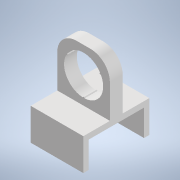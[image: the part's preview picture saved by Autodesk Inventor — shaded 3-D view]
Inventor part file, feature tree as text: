
AUTODESK INVENTOR PART (.ipt)
format: ipt  version: 2022 (Build 260153000, 153)  size: 176,128 bytes
history: native  units: mm
features: other x5, reference x4, extrude x3, sketch x3, fillet x1
ambient origin geometry x8: Origin, YZ Plane, XZ Plane, XY Plane, X Axis, Y Axis, Z Axis, Center Point
bodies: Solid1 (feature_tree)
feature tree (16):
  extrude  "Extrusion1"  Depth=0.3mm
  extrude  "Extrusion2"  Depth=18.0mm
  fillet  "Fillet2"  Radius=3.0mm
  extrude  "Extrusion4"  Depth=11.0mm TaperAngle=0.0deg
  sketch  "Sketch2"  dims[d0=0.3mm d1=0.3mm]
  reference  "Reference1"
  reference  "Reference2"
  reference  "Reference3"
  sketch  "Sketch5"  dims[d2=3.0mm d3=18.0mm d4=3.0mm]
  sketch  "Sketch7"  dims[d11=3.5mm d12=15.0mm d13=15.0mm d14=0.0mm d15=0.0mm d33=7.3mm d34=30.0mm d35=15.15mm d36=22.3mm d37=1.0mm d38=30.0mm d40=360.0deg d42=15.0mm d43=15.0mm d44=11.15mm d45=10.0mm d46=0.0mm d47=11.0mm d50=40.0mm d51=0.0mm]
  reference  "Reference6"
  other  "<userpath>\OneDrive\Escritorio\Mini_Proyecto_Diseno\Diseno_18012\Modelo_MPD\Carril.iam"
  other  "Carril.iam"
  other  "Base_Carril:1"
  other  "Lateral_Carril:2"
  other  "Lateral_Carril:1"
